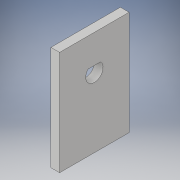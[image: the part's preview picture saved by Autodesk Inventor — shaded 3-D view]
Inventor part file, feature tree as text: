
AUTODESK INVENTOR PART (.ipt)
format: ipt  version: 2017 (Build 210142000, 142)  size: 111,104 bytes
history: native  units: in
note: dims shown in document units (in); Inventor stores cm internally (conversion verified against a paired STEP export)
features: sketch x3, extrude x2, hole x1, projected_geometry x1
ambient origin geometry x8: Origin, YZ Plane, XZ Plane, XY Plane, X Axis, Y Axis, Z Axis, Center Point
bodies: Solid1 (feature_tree)
feature tree (7):
  extrude  "Extrusion1"  Depth=2.0in
  hole  "Hole1"  [1 undecoded]
  extrude  "Extrusion2"  Depth=0.25in
  sketch  "Sketch1"  dims[d0=3.0in d1=2.0in]
  sketch  "Sketch2"  dims[d2=0.25in d3=0.0in d4=2.0in]
  sketch  "Sketch3"  dims[d5=1.0in d6=1.0in d7=0.5in d8=0.75in d9=0.375in d10=0.25in d11=0.5635in d12=1.0in d13=0.8108in d14=0.175in d15=0.25in d16=0.0in]
  projected_geometry  "Projected Loop1"
note: 1 required parameter value undecoded (feature->parameter linkage not recoverable at this tier; creation-order binding heuristic only, values carry confidence <= 0.55)
